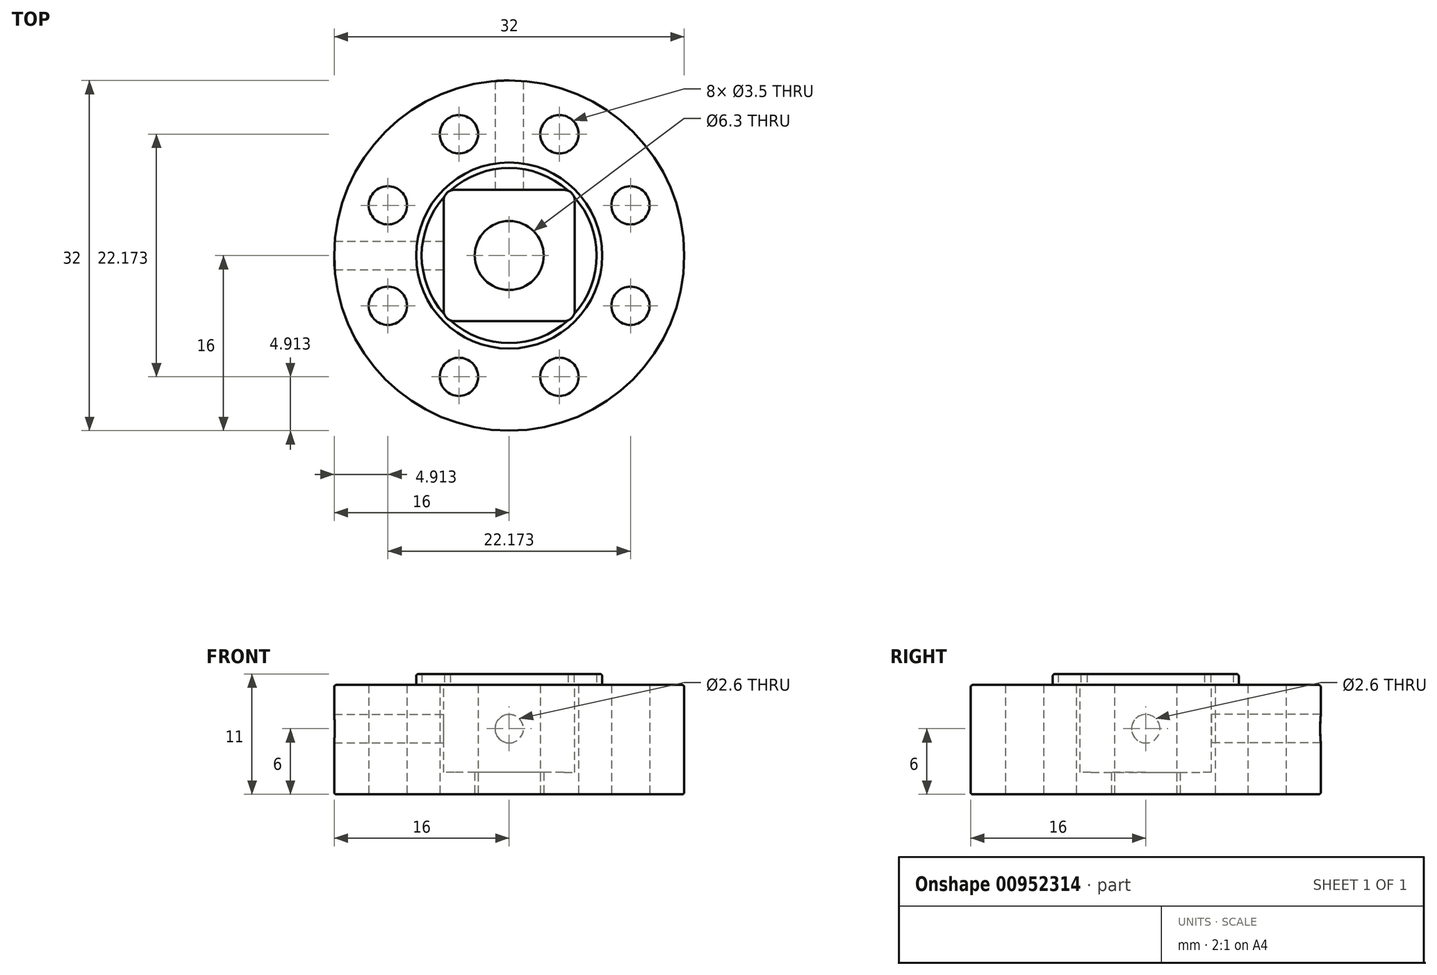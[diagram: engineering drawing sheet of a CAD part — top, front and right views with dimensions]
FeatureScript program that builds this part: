
annotation { "Feature Type Name" : "Feature", "Feature Type Description" : "" }
export const myFeature = defineFeature(function(context is Context, id is Id, definition is map)
    precondition{}
    {
        {
            var Q0;
            Q0=qCreatedBy(makeId("Top.planeOp"),FACE);
            var sketch = newSketch(context, id + "F0", { "sketchPlane" : qUnion([Q0])});
            skCircle(sketch, "E0", {"center": v(0, 0) * mm, "radius": 16 * mm});
            skSolve(sketch);
        }
        {
            var Q0;
            Q0 = qSketchRegion(id + "F0", true);
            extrude(context, id + "F1", {"entities" : qUnion([Q0]), "depth" : 10 * mm, "offsetDistance" : 25 * mm});
        }
        {
            var Q0;
            Q0=makeQuery(id+"F1.opExtrude","CAP_FACE",FACE,{"disambiguationData":[OSD([sQuery(id+"F0.wireOp",EDGE,"E0")])],"isStart":false});
            var sketch = newSketch(context, id + "F2", { "sketchPlane" : qUnion([Q0])});
            skLineSegment(sketch, "E1.bottom", {"start": v(6, -6) * mm, "end": v(-6, -6) * mm});
            skLineSegment(sketch, "E1.top", {"start": v(6, 6) * mm, "end": v(-6, 6) * mm});
            skLineSegment(sketch, "E1.left", {"start": v(6, -6) * mm, "end": v(6, 6) * mm});
            skLineSegment(sketch, "E1.right", {"start": v(-6, -6) * mm, "end": v(-6, 6) * mm});
            skPoint(sketch, "E1.middle", {"position": v(0, 0) * mm});
            skSolve(sketch);
        }
        {
            var Q0;
            Q0 = qSketchRegion(id + "F2", true);
            extrude(context, id + "F3", {"entities" : qUnion([Q0]), "operationType" : NewBodyOperationType.REMOVE, "oppositeDirection" : true, "depth" : 8 * mm, "offsetDistance" : 25 * mm});
        }
        {
            var Q0;
            Q0=makeQuery(id+"F1.opExtrude","CAP_FACE",FACE,{"disambiguationData":[OSD([sQuery(id+"F0.wireOp",EDGE,"E0")])],"isStart":true});
            var sketch = newSketch(context, id + "F4", { "sketchPlane" : qUnion([Q0])});
            skCircle(sketch, "E2", {"center": v(0, 0) * mm, "radius": 3.15 * mm});
            skSolve(sketch);
        }
        {
            var Q0;
            Q0 = qSketchRegion(id + "F4", true);
            var Q1;
            Q1=makeQuery(id+"F3.boolean.opBoolean","COPY",FACE,{"derivedFrom":makeQuery(id+"F3.opExtrude","CAP_FACE",FACE,{"disambiguationData":[OSD([sQuery(id+"F2.wireOp",EDGE,"E1.bottom"),sQuery(id+"F2.wireOp",EDGE,"E1.top"),sQuery(id+"F2.wireOp",EDGE,"E1.left"),sQuery(id+"F2.wireOp",EDGE,"E1.right")])],"isStart":false})});
            extrude(context, id + "F5", {"entities" : qUnion([Q0]), "operationType" : NewBodyOperationType.REMOVE, "endBound" : BoundingType.UP_TO_SURFACE, "oppositeDirection" : true, "depth" : 25 * mm, "endBoundEntityFace" : qUnion([Q1]), "offsetDistance" : 25 * mm});
        }
        {
            var Q0;
            Q0=makeQuery(id+"F1.opExtrude","CAP_FACE",FACE,{"disambiguationData":[OSD([sQuery(id+"F0.wireOp",EDGE,"E0")])],"isStart":true});
            var sketch = newSketch(context, id + "F6", { "sketchPlane" : qUnion([Q0])});
            skCircle(sketch, "E3", {"center": v(11.09, 4.6) * mm, "radius": 1.75 * mm});
            skCircle(sketch, "E4.1.0", {"center": v(4.6, 11.09) * mm, "radius": 1.75 * mm});
            skCircle(sketch, "E4.2.0", {"center": v(-4.6, 11.09) * mm, "radius": 1.75 * mm});
            skCircle(sketch, "E4.3.0", {"center": v(-11.09, 4.6) * mm, "radius": 1.75 * mm});
            skCircle(sketch, "E4.4.0", {"center": v(-11.09, -4.6) * mm, "radius": 1.75 * mm});
            skCircle(sketch, "E4.5.0", {"center": v(-4.6, -11.09) * mm, "radius": 1.75 * mm});
            skCircle(sketch, "E4.6.0", {"center": v(4.6, -11.09) * mm, "radius": 1.75 * mm});
            skCircle(sketch, "E4.7.0", {"center": v(11.09, -4.6) * mm, "radius": 1.75 * mm});
            skPoint(sketch, "E4.center", {"position": v(0, 0) * mm});
            skLineSegment(sketch, "E5", {"start": v(11.09, 4.6) * mm, "end": v(0, 0) * mm});
            skSolve(sketch);
        }
        {
            var Q0;
            Q0 = qSketchRegion(id + "F6", true);
            var Q1;
            Q1=makeQuery(id+"F1.opExtrude","CAP_FACE",FACE,{"disambiguationData":[OSD([sQuery(id+"F0.wireOp",EDGE,"E0")])],"isStart":false});
            extrude(context, id + "F7", {"entities" : qUnion([Q0]), "operationType" : NewBodyOperationType.REMOVE, "endBound" : BoundingType.UP_TO_SURFACE, "oppositeDirection" : true, "depth" : 25 * mm, "endBoundEntityFace" : qUnion([Q1]), "offsetDistance" : 25 * mm});
        }
        {
            var Q0;
            Q0=qCreatedBy(makeId("Front.planeOp"),FACE);
            var sketch = newSketch(context, id + "F8", { "sketchPlane" : qUnion([Q0])});
            skCircle(sketch, "E6", {"center": v(0, 6) * mm, "radius": 1.3 * mm});
            skSolve(sketch);
        }
        {
            var Q0;
            Q0 = qSketchRegion(id + "F8", true);
            extrude(context, id + "F9", {"entities" : qUnion([Q0]), "operationType" : NewBodyOperationType.REMOVE, "oppositeDirection" : true, "depth" : 25 * mm, "offsetDistance" : 25 * mm});
        }
        {
            var Q0;
            Q0=qCreatedBy(makeId("Right.planeOp"),FACE);
            var sketch = newSketch(context, id + "F10", { "sketchPlane" : qUnion([Q0])});
            skCircle(sketch, "E7", {"center": v(0, 6) * mm, "radius": 1.3 * mm});
            skSolve(sketch);
        }
        {
            var Q0;
            Q0 = qSketchRegion(id + "F10", true);
            extrude(context, id + "F11", {"entities" : qUnion([Q0]), "operationType" : NewBodyOperationType.REMOVE, "oppositeDirection" : true, "depth" : 25 * mm, "offsetDistance" : 25 * mm});
        }
        {
            var Q0;
            Q0=makeQuery(id+"F1.opExtrude","CAP_FACE",FACE,{"disambiguationData":[OSD([sQuery(id+"F0.wireOp",EDGE,"E0")])],"isStart":false});
            var sketch = newSketch(context, id + "F12", { "sketchPlane" : qUnion([Q0])});
            skCircle(sketch, "E8", {"center": v(0, 0) * mm, "radius": 8.5 * mm});
            skCircle(sketch, "E9", {"center": v(0, 0) * mm, "radius": 8 * mm});
            skSolve(sketch);
        }
        {
            var Q0;
            {var subQ0=sQuery(id+"F12.wireOp",EDGE,"E9");var subQ1=makeQuery(id+"F3.boolean.opBoolean","COPY",EDGE,{"derivedFrom":makeQuery(id+"F3.opExtrude","CAP_EDGE",EDGE,{"disambiguationData":[OSD([sQuery(id+"F2.wireOp",EDGE,"E1.bottom")])],"isStart":true})});var subQ2=makeQuery(id+"F12.imprint","INTERSECT",VERTEX,{"disambiguationData":[OD(0.0)],"derivedFrom":[subQ1,subQ0]});Q0=makeQuery(id+"F12.imprint","IMPRINT",FACE,{"disambiguationData":[TD([[makeQuery(id+"F12.imprint","IMPRINT",EDGE,{"disambiguationData":[TD([[subQ2,-1.0]])],"derivedFrom":subQ0}),1.0]])]});}
            var Q1;
            {var subQ0=sQuery(id+"F12.wireOp",EDGE,"E9");var subQ1=makeQuery(id+"F3.boolean.opBoolean","COPY",EDGE,{"derivedFrom":makeQuery(id+"F3.opExtrude","CAP_EDGE",EDGE,{"disambiguationData":[OSD([sQuery(id+"F2.wireOp",EDGE,"E1.right")])],"isStart":true})});var subQ2=makeQuery(id+"F12.imprint","INTERSECT",VERTEX,{"disambiguationData":[OD(0.0)],"derivedFrom":[subQ1,subQ0]});Q1=makeQuery(id+"F12.imprint","IMPRINT",FACE,{"disambiguationData":[TD([[makeQuery(id+"F12.imprint","IMPRINT",EDGE,{"disambiguationData":[TD([[subQ2,-1.0]])],"derivedFrom":subQ0}),1.0]])]});}
            var Q2;
            {var subQ0=sQuery(id+"F12.wireOp",EDGE,"E9");var subQ1=makeQuery(id+"F3.boolean.opBoolean","COPY",EDGE,{"derivedFrom":makeQuery(id+"F3.opExtrude","CAP_EDGE",EDGE,{"disambiguationData":[OSD([sQuery(id+"F2.wireOp",EDGE,"E1.top")])],"isStart":true})});var subQ2=makeQuery(id+"F12.imprint","INTERSECT",VERTEX,{"disambiguationData":[OD(0.0)],"derivedFrom":[subQ1,subQ0]});Q2=makeQuery(id+"F12.imprint","IMPRINT",FACE,{"disambiguationData":[TD([[makeQuery(id+"F12.imprint","IMPRINT",EDGE,{"disambiguationData":[TD([[subQ2,-1.0]])],"derivedFrom":subQ0}),1.0]])]});}
            var Q3;
            {var subQ0=sQuery(id+"F12.wireOp",EDGE,"E9");var subQ1=makeQuery(id+"F3.boolean.opBoolean","COPY",EDGE,{"derivedFrom":makeQuery(id+"F3.opExtrude","CAP_EDGE",EDGE,{"disambiguationData":[OSD([sQuery(id+"F2.wireOp",EDGE,"E1.left")])],"isStart":true})});var subQ2=makeQuery(id+"F12.imprint","INTERSECT",VERTEX,{"disambiguationData":[OD(0.0)],"derivedFrom":[subQ1,subQ0]});Q3=makeQuery(id+"F12.imprint","IMPRINT",FACE,{"disambiguationData":[TD([[makeQuery(id+"F12.imprint","IMPRINT",EDGE,{"disambiguationData":[TD([[subQ2,1.0]])],"derivedFrom":subQ0}),1.0]])]});}
            var Q4;
            Q4=makeQuery(id+"F12.imprint","IMPRINT",FACE,{"disambiguationData":[TD([[makeQuery(id+"F12.imprint","IMPRINT",EDGE,{"derivedFrom":sQuery(id+"F12.wireOp",EDGE,"E8")}),1.0]])]});
            extrude(context, id + "F13", {"entities" : qUnion([Q0, Q1, Q2, Q3, Q4]), "operationType" : NewBodyOperationType.ADD, "depth" : 1 * mm, "offsetDistance" : 25 * mm});
        }
        {
            var Q0;
            {var subQ0=sQuery(id+"F2.wireOp",EDGE,"E1.right");var subQ1=sQuery(id+"F2.wireOp",EDGE,"E1.bottom");Q0=makeQuery(id+"F13.boolean.opBoolean","MERGE",EDGE,{"derivedFrom":[makeQuery(id+"F3.boolean.opBoolean","COPY",EDGE,{"derivedFrom":makeQuery(id+"F3.opExtrude","SWEPT_EDGE",EDGE,{"disambiguationData":[OSD([subQ1,subQ0])]})}),makeQuery(id+"F13.opExtrude","SWEPT_EDGE",EDGE,{"disambiguationData":[OSD([subQ1,subQ0])]})]});}
            var Q1;
            {var subQ0=sQuery(id+"F2.wireOp",EDGE,"E1.left");var subQ1=sQuery(id+"F2.wireOp",EDGE,"E1.bottom");Q1=makeQuery(id+"F13.boolean.opBoolean","MERGE",EDGE,{"derivedFrom":[makeQuery(id+"F3.boolean.opBoolean","COPY",EDGE,{"derivedFrom":makeQuery(id+"F3.opExtrude","SWEPT_EDGE",EDGE,{"disambiguationData":[OSD([subQ1,subQ0])]})}),makeQuery(id+"F13.opExtrude","SWEPT_EDGE",EDGE,{"disambiguationData":[OSD([subQ1,subQ0])]})]});}
            var Q2;
            {var subQ0=sQuery(id+"F2.wireOp",EDGE,"E1.left");var subQ1=sQuery(id+"F2.wireOp",EDGE,"E1.top");Q2=makeQuery(id+"F13.boolean.opBoolean","MERGE",EDGE,{"derivedFrom":[makeQuery(id+"F3.boolean.opBoolean","COPY",EDGE,{"derivedFrom":makeQuery(id+"F3.opExtrude","SWEPT_EDGE",EDGE,{"disambiguationData":[OSD([subQ1,subQ0])]})}),makeQuery(id+"F13.opExtrude","SWEPT_EDGE",EDGE,{"disambiguationData":[OSD([subQ1,subQ0])]})]});}
            var Q3;
            {var subQ0=sQuery(id+"F2.wireOp",EDGE,"E1.right");var subQ1=sQuery(id+"F2.wireOp",EDGE,"E1.top");Q3=makeQuery(id+"F13.boolean.opBoolean","MERGE",EDGE,{"derivedFrom":[makeQuery(id+"F3.boolean.opBoolean","COPY",EDGE,{"derivedFrom":makeQuery(id+"F3.opExtrude","SWEPT_EDGE",EDGE,{"disambiguationData":[OSD([subQ1,subQ0])]})}),makeQuery(id+"F13.opExtrude","SWEPT_EDGE",EDGE,{"disambiguationData":[OSD([subQ1,subQ0])]})]});}
            fillet(context, id + "F14", {"entities" : qUnion([Q0, Q1, Q2, Q3]), "radius" : 1 * mm, "tangentPropagation" : true, "allowEdgeOverflow" : false});
        }
        {
            var Q0;
            Q0=makeQuery(id+"F1.opExtrude","CAP_EDGE",EDGE,{"disambiguationData":[OSD([sQuery(id+"F0.wireOp",EDGE,"E0")])],"isStart":false});
            var Q1;
            Q1=makeQuery(id+"F1.opExtrude","CAP_EDGE",EDGE,{"disambiguationData":[OSD([sQuery(id+"F0.wireOp",EDGE,"E0")])],"isStart":true});
            var Q2;
            Q2=makeQuery(id+"F13.opExtrude","CAP_EDGE",EDGE,{"disambiguationData":[OSD([sQuery(id+"F12.wireOp",EDGE,"E8")])],"isStart":false});
            var Q3;
            Q3=makeQuery(id+"F13.opExtrude","CAP_EDGE",EDGE,{"disambiguationData":[OSD([sQuery(id+"F2.wireOp",EDGE,"E1.bottom")])],"isStart":false});
            fillet(context, id + "F15", {"entities" : qUnion([Q0, Q1, Q2, Q3]), "radius" : 0.2 * mm, "tangentPropagation" : true, "allowEdgeOverflow" : false});
        }
    });
